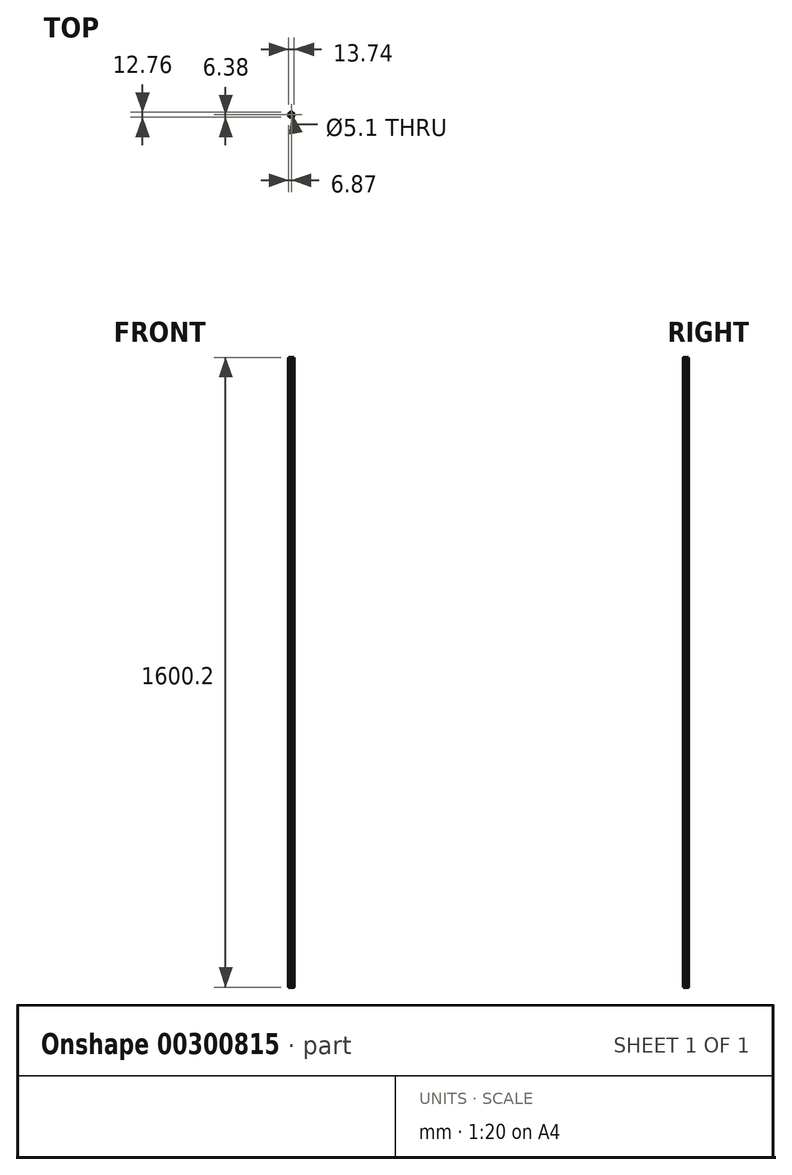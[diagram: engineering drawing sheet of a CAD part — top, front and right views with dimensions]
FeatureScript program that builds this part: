
annotation { "Feature Type Name" : "Feature", "Feature Type Description" : "" }
export const myFeature = defineFeature(function(context is Context, id is Id, definition is map)
    precondition{}
    {
        {
            var Q0;
            Q0=qCreatedBy(makeId("Top.planeOp"),FACE);
            var sketch = newSketch(context, id + "F0", { "sketchPlane" : qUnion([Q0])});
            skArc(sketch, "E0.0.0", {"start": v(2.56, 6.38) * mm, "mid": v(3.44, 5.95) * mm, "end": v(4.24, 5.4) * mm});
            skLineSegment(sketch, "E0.0.1", {"start": v(4.24, 5.4) * mm, "end": v(6.8, 0.97) * mm});
            skArc(sketch, "E0.0.2", {"start": v(6.8, 0.97) * mm, "mid": v(6.87, 0) * mm, "end": v(6.8, -0.97) * mm});
            skLineSegment(sketch, "E0.0.3", {"start": v(6.8, -0.97) * mm, "end": v(4.24, -5.4) * mm});
            skArc(sketch, "E0.0.4", {"start": v(4.24, -5.4) * mm, "mid": v(3.44, -5.95) * mm, "end": v(2.56, -6.38) * mm});
            skLineSegment(sketch, "E0.0.5", {"start": v(2.56, -6.38) * mm, "end": v(-2.56, -6.38) * mm});
            skArc(sketch, "E0.0.6", {"start": v(-2.56, -6.38) * mm, "mid": v(-3.44, -5.95) * mm, "end": v(-4.24, -5.4) * mm});
            skLineSegment(sketch, "E0.0.7", {"start": v(-4.24, -5.4) * mm, "end": v(-6.8, -0.97) * mm});
            skArc(sketch, "E0.0.8", {"start": v(-6.8, -0.97) * mm, "mid": v(-6.87, 0) * mm, "end": v(-6.8, 0.97) * mm});
            skLineSegment(sketch, "E0.0.9", {"start": v(-6.8, 0.97) * mm, "end": v(-4.24, 5.4) * mm});
            skArc(sketch, "E0.0.10", {"start": v(-4.24, 5.4) * mm, "mid": v(-3.44, 5.95) * mm, "end": v(-2.56, 6.38) * mm});
            skLineSegment(sketch, "E0.0.11", {"start": v(-2.56, 6.38) * mm, "end": v(2.56, 6.38) * mm});
            skCircle(sketch, "E1.0", {"center": v(0, 0) * mm, "radius": 2.55 * mm});
            skSolve(sketch);
        }
        {
            var Q0;
            Q0 = qSketchRegion(id + "F0", true);
            extrude(context, id + "F1", {"entities" : qUnion([Q0]), "depth" : 1600.2 * mm});
        }
    });
